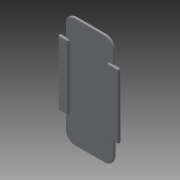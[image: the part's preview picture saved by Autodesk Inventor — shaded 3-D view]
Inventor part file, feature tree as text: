
AUTODESK INVENTOR PART (.ipt)
format: ipt  version: 2015 (Build 190159000, 159)  size: 194,048 bytes
history: native  units: mm
features: extrude x4, fillet x3, sketch x2, chamfer x1
ambient origin geometry x8: Origin, YZ Plane, XZ Plane, XY Plane, X Axis, Y Axis, Z Axis, Center Point
bodies: Solid1 (feature_tree)
feature tree (10):
  extrude  "Extrusion1"  Depth=5.0mm
  fillet  "Fillet1"  Radius=5.0mm
  extrude  "Extrusion3"  Depth=2.0mm
  extrude  "Extrusion4"  Depth=10.0mm
  extrude  "Extrusion5"  Depth=2.0mm
  chamfer  "Chamfer2"  Distance=3.0mm
  fillet  "Fillet3"  Radius=136.0mm
  fillet  "Fillet4"  Radius=6.0mm
  sketch  "Sketch3"  dims[d0=231.3mm d1=101.2mm d2=5.0mm d3=0.0mm]
  sketch  "Sketch4"  dims[d4=20.0mm d14=45.0mm d18=10.0mm d19=136.0mm d20=3.0mm d21=0.0mm d22=136.0mm d23=6.0mm d24=13.0mm d25=0.0mm d26=136.0mm d27=6.0mm d28=13.0mm d29=0.0mm d30=3.0mm d31=2.0mm d32=45.0deg d33=3.0mm d34=2.0mm]
